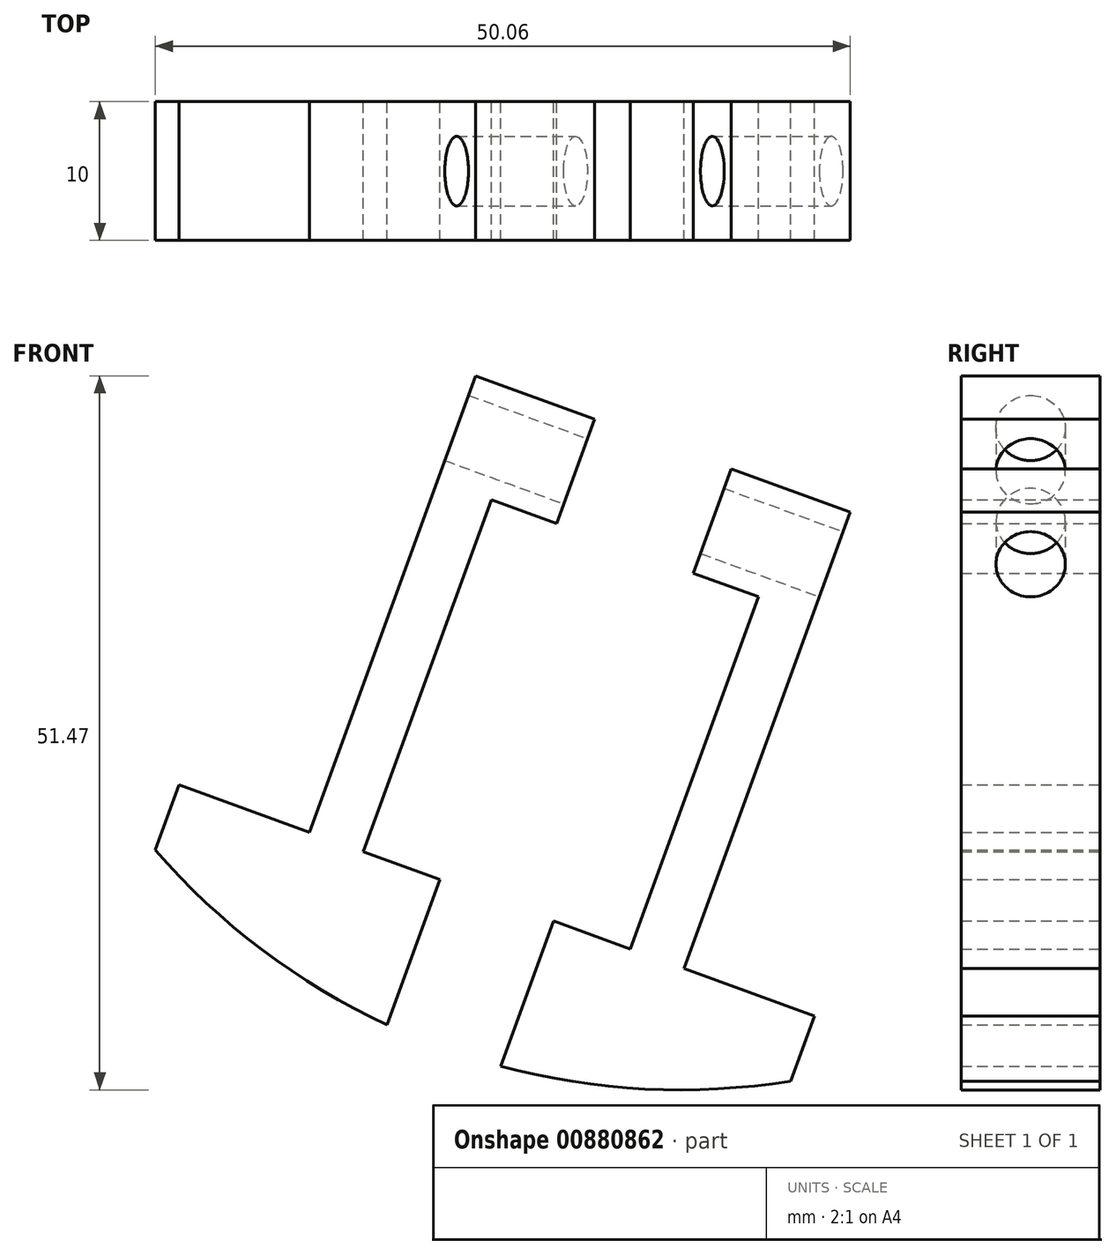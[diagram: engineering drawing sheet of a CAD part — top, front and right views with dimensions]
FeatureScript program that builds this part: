
annotation { "Feature Type Name" : "Feature", "Feature Type Description" : "" }
export const myFeature = defineFeature(function(context is Context, id is Id, definition is map)
    precondition{}
    {
        {
            var Q0;
            Q0=qCreatedBy(makeId("Front.planeOp"),FACE);
            var sketch = newSketch(context, id + "F0", { "sketchPlane" : qUnion([Q0])});
            skArc(sketch, "E0", {"start": v(-37.82, 17.3) * mm, "mid": v(-30.14, 10.1) * mm, "end": v(-21.13, 4.68) * mm});
            skLineSegment(sketch, "E1", {"start": v(0, 50) * mm, "end": v(-17.1, 3.02) * mm, "construction": true});
            skLineSegment(sketch, "E2", {"start": v(0, 50) * mm, "end": v(0, 0) * mm, "construction": true});
            skLineSegment(sketch, "E3", {"start": v(0, 50) * mm, "end": v(-21.13, 4.68) * mm, "construction": true});
            skLineSegment(sketch, "E4", {"start": v(-21.13, 4.68) * mm, "end": v(-17.32, 15.16) * mm});
            skLineSegment(sketch, "E5", {"start": v(-36.11, 22) * mm, "end": v(-37.82, 17.3) * mm});
            skLineSegment(sketch, "E6", {"start": v(-36.11, 22) * mm, "end": v(-17.32, 15.16) * mm});
            skLineSegment(sketch, "E7", {"start": v(-26.72, 18.58) * mm, "end": v(-14.75, 51.47) * mm});
            skLineSegment(sketch, "E8", {"start": v(-14.75, 51.47) * mm, "end": v(-6.18, 48.35) * mm});
            skLineSegment(sketch, "E9", {"start": v(-6.18, 48.35) * mm, "end": v(-8.92, 40.83) * mm});
            skLineSegment(sketch, "E10", {"start": v(-8.92, 40.83) * mm, "end": v(-13.62, 42.54) * mm});
            skLineSegment(sketch, "E11", {"start": v(-13.62, 42.54) * mm, "end": v(-22.85, 17.17) * mm});
            skLineSegment(sketch, "E12.MirrorCS", {"start": v(3.68, 44.76) * mm, "end": v(0.94, 37.24) * mm});
            skLineSegment(sketch, "E13.MirrorCS", {"start": v(12.24, 41.64) * mm, "end": v(3.68, 44.76) * mm});
            skLineSegment(sketch, "E14.MirrorCS", {"start": v(0.27, 8.76) * mm, "end": v(12.24, 41.64) * mm});
            skLineSegment(sketch, "E15.MirrorCS", {"start": v(5.64, 35.53) * mm, "end": v(-3.6, 10.16) * mm});
            skLineSegment(sketch, "E16.MirrorCS", {"start": v(0.94, 37.24) * mm, "end": v(5.64, 35.53) * mm});
            skLineSegment(sketch, "E17.MirrorCS", {"start": v(9.66, 5.34) * mm, "end": v(-9.13, 12.18) * mm});
            skLineSegment(sketch, "E18.MirrorCS", {"start": v(-12.94, 1.7) * mm, "end": v(-9.13, 12.18) * mm});
            skLineSegment(sketch, "E19.MirrorCS", {"start": v(9.66, 5.34) * mm, "end": v(7.95, 0.64) * mm});
            skArc(sketch, "E20.trimOffspring", {"start": v(-12.94, 1.7) * mm, "mid": v(-2.55, 0.07) * mm, "end": v(7.95, 0.64) * mm});
            skSolve(sketch);
        }
        {
            var Q0;
            Q0 = qSketchRegion(id + "F0", true);
            extrude(context, id + "F1", {"entities" : qUnion([Q0]), "depth" : 10 * mm, "offsetDistance" : 25 * mm});
        }
        {
            var Q0;
            Q0=makeQuery(id+"F1.opExtrude","SWEPT_FACE",FACE,{"disambiguationData":[OSD([sQuery(id+"F0.wireOp",EDGE,"E9")])]});
            var sketch = newSketch(context, id + "F2", { "sketchPlane" : qUnion([Q0])});
            skLineSegment(sketch, "E21", {"start": v(-10, 39.32) * mm, "end": v(0, 39.32) * mm, "construction": true});
            skCircle(sketch, "E22", {"center": v(-5, 39.32) * mm, "radius": 2.5 * mm});
            skLineSegment(sketch, "E23", {"start": v(-5, 43.32) * mm, "end": v(-5, 35.32) * mm, "construction": true});
            skSolve(sketch);
        }
        {
            var Q0;
            Q0 = qSketchRegion(id + "F2", true);
            var Q1;
            Q1=makeQuery(id+"F1.opExtrude","SWEPT_FACE",FACE,{"disambiguationData":[OSD([sQuery(id+"F0.wireOp",EDGE,"E14.MirrorCS")])]});
            extrude(context, id + "F3", {"entities" : qUnion([Q0]), "operationType" : NewBodyOperationType.REMOVE, "endBound" : BoundingType.THROUGH_ALL, "oppositeDirection" : true, "depth" : 25 * mm, "offsetDistance" : 25 * mm, "hasSecondDirection" : true, "secondDirectionBound" : SecondDirectionBoundingType.UP_TO_SURFACE, "secondDirectionOppositeDirection" : false, "secondDirectionDepth" : 25 * mm, "secondDirectionBoundEntityFace" : qUnion([Q1])});
        }
    });
